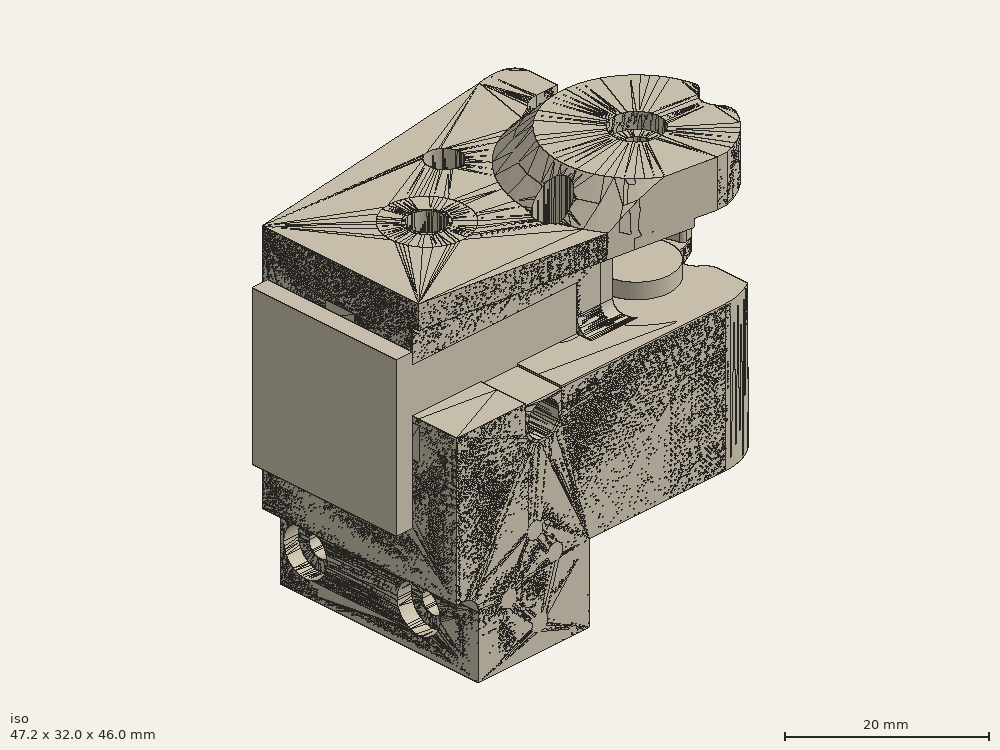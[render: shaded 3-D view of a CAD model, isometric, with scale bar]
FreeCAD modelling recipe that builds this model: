
FCSTD DOCUMENT  (FreeCAD 0.18R16146 (Git))
Label: carrier-right-2
License: All rights reserved
LicenseURL: http://en.wikipedia.org/wiki/All_rights_reserved
objects: Part::Cylinder×19, Part::Box×10, Part::Cut×10, Part::MultiFuse×9, Part::Feature×7, Part::Chamfer×6, Mesh::Feature×1
note: 61 computed .brp shape members not serialized (recipe doc carries the construction recipe); baked Part::Feature solids carry a one-line shape summary decoded from their .brp

FEATURE [Part::Box] Box003  label="Cube003"
  AttacherType = Attacher::AttachEngine3D
  Height = 2
  Length = 9
  Placement = pos=(-20.93,14.39,15.2) rot=(0,0,1;0rad)
  Width = 4
FEATURE [Part::Box] Box004  label="Cube004"
  AttacherType = Attacher::AttachEngine3D
  Height = 2
  Length = 9
  Placement = pos=(-5.93,14.39,15.2) rot=(0,0,1;0rad)
  Width = 4
FEATURE [Part::Box] Box005  label="Cube005"
  AttacherType = Attacher::AttachEngine3D
  Height = 2
  Length = 9
  Placement = pos=(-5.93,14.39,35.2) rot=(0,0,1;0rad)
  Width = 4
FEATURE [Part::Box] Box006  label="Cube006"
  AttacherType = Attacher::AttachEngine3D
  Height = 2
  Length = 9
  Placement = pos=(-20.93,14.39,35.2) rot=(0,0,1;0rad)
  Width = 4
FEATURE [Part::Box] Box007  label="Cube007"
  AttacherType = Attacher::AttachEngine3D
  Height = 4.2
  Length = 9
  Placement = pos=(-20.93,5.39,24) rot=(0,0,1;0rad)
  Width = 2
FEATURE [Part::Box] Box008  label="Cube008"
  AttacherType = Attacher::AttachEngine3D
  Height = 4.2
  Length = 7
  Placement = pos=(-5.93,5.39,24) rot=(0,0,1;0rad)
  Width = 2
FEATURE [Part::Chamfer] Chamfer
  Base = -> Box008
  Edges = 1 edges r=1: [Edge11]
FEATURE [Part::Chamfer] Chamfer001
  Base = -> Box007
  Edges = 1 edges r=1: [Edge11]
FEATURE [Part::MultiFuse] Fusion
  Shapes = -> [Chamfer001,Chamfer,Box006,Box005,Box004,Box003]
FEATURE [Part::Feature] Part__Feature199  label="Y_Carriage_RIGHT_Body (1)"
  Placement = pos=(-664.031,179.424,-461.938) rot=(1,0,0;1.5708rad)
  shape: bbox 48.82 x 34.51 x 45.95 mm, 173 faces (baked)
FEATURE [Part::Cylinder] Cylinder  label="ois-1"
  Angle = 360
  AttacherType = Attacher::AttachEngine3D
  Height = 2
  Placement = pos=(13.89,10.12,28.95) rot=(0,0,1;0rad)
  Radius = 4.5
FEATURE [Part::Cylinder] Cylinder009
  Angle = 360
  AttacherType = Attacher::AttachEngine3D
  Height = 0.75
  Placement = pos=(13.89,10.12,28.7) rot=(0,0,1;0rad)
  Radius = 1.5
FEATURE [Part::Cylinder] Cylinder010
  Angle = 360
  AttacherType = Attacher::AttachEngine3D
  Height = 0.75
  Placement = pos=(13.89,10.12,28.7) rot=(0,0,1;0rad)
  Radius = 3.5
FEATURE [Part::Cylinder] Cylinder011
  Angle = 360
  AttacherType = Attacher::AttachEngine3D
  Height = 0.75
  Placement = pos=(16.18,23.33,17.7) rot=(0,0,1;0rad)
  Radius = 3
FEATURE [Part::Cylinder] Cylinder012
  Angle = 360
  AttacherType = Attacher::AttachEngine3D
  Height = 11
  Placement = pos=(16.18,23.33,17.7) rot=(0,0,1;0rad)
  Radius = 10
FEATURE [Part::Cylinder] Cylinder013
  Angle = 360
  AttacherType = Attacher::AttachEngine3D
  Height = 0.75
  Placement = pos=(16.18,23.33,17.7) rot=(0,0,1;0rad)
  Radius = 1.5
FEATURE [Mesh::Feature] carrier_right  label="carrier-right"
FEATURE [Part::Feature] Part__Feature113  label="Y_CarriageHT_RIGHT_Body (1)"
  Placement = pos=(-664.031,179.424,-461.938) rot=(1,0,0;1.5708rad)
  shape: bbox 48.82 x 34.51 x 45.95 mm, 188 faces (baked)
FEATURE [Part::Box] Box010  label="Cube010"
  AttacherType = Attacher::AttachEngine3D
  Height = 20
  Length = 25
  Placement = pos=(-23.16,6.39,16.2) rot=(0,0,1;0rad)
  Width = 20
FEATURE [Part::Cylinder] Cylinder015
  Angle = 360
  AttacherType = Attacher::AttachEngine3D
  Height = 2
  Placement = pos=(13.89,10.12,38.2) rot=(0,0,1;0rad)
  Radius = 4.5
FEATURE [Part::Cylinder] Cylinder016
  Angle = 360
  AttacherType = Attacher::AttachEngine3D
  Height = 2
  Placement = pos=(13.89,10.12,28.7) rot=(0,0,1;0rad)
  Radius = 8
FEATURE [Part::Cylinder] Cylinder017
  Angle = 360
  AttacherType = Attacher::AttachEngine3D
  Height = 2
  Placement = pos=(13.89,10.12,38.2) rot=(0,0,1;0rad)
  Radius = 8
FEATURE [Part::Cut] Cut006003004
  Base = -> Cylinder010
  Tool = -> Cylinder009
FEATURE [Part::Feature] Cut006003004001  label="Cut006003005"
  Placement = pos=(0,0,10.75) rot=(0,0,1;0rad)
  shape: bbox 7 x 7 x 0.75 mm, 4 faces (baked)
FEATURE [Part::Chamfer] Chamfer002
  Base = -> Cut006003004001
  Edges = 1 edges r=0.5: [Edge3]
  Placement = pos=(0,0,0.1) rot=(0,0,1;0rad)
FEATURE [Part::Chamfer] Chamfer003
  Base = -> Cut006003004
  Edges = 1 edges r=0.5: [Edge1]
  Placement = pos=(0,0,-0.1) rot=(0,0,1;0rad)
FEATURE [Part::Cylinder] Cylinder014
  Angle = 360
  AttacherType = Attacher::AttachEngine3D
  Height = 5
  Placement = pos=(20.97,23.88,17) rot=(0,0,1;1.5708rad)
  Radius = 3
FEATURE [Part::Cut] Cut006003004003
  Base = -> Cylinder011
  Tool = -> Cylinder013
FEATURE [Part::Feature] Cut006003004003001  label="Cut006003004004"
  Placement = pos=(0,0,10.6) rot=(0,0,1;0rad)
  shape: bbox 6 x 6 x 0.75 mm, 4 faces (baked)
FEATURE [Part::Feature] Cut006003004003002  label="Cut006003004005"
  Placement = pos=(0,0,-0.35) rot=(0,0,1;0rad)
  shape: bbox 6 x 6 x 0.75 mm, 4 faces (baked)
FEATURE [Part::Chamfer] Chamfer004
  Base = -> Cut006003004003002
  Edges = 1 edges r=0.5: [Edge1]
FEATURE [Part::Cut] Cut006003004003003
  Base = -> Chamfer004
  Tool = -> Cylinder014
FEATURE [Part::Chamfer] Chamfer005
  Base = -> Cut006003004003001
  Edges = 1 edges r=0.5: [Edge3]
FEATURE [Part::Box] Box  label="Cube"
  AttacherType = Attacher::AttachEngine3D
  Height = 10
  Length = 10
  Placement = pos=(19.07,19.6,23.8) rot=(0,0,1;0rad)
  Width = 10
FEATURE [Part::Cut] Cut006003004003004
  Base = -> Chamfer005
  Tool = -> Box
FEATURE [Part::MultiFuse] Fusion001
  Shapes = -> [Cut006003004003004,Cut006003004003003,Chamfer002,Chamfer003]
FEATURE [Part::Feature] Fusion003001_solid  label="rev-1-exp"
  shape: bbox 48.82 x 34.51 x 45.95 mm, 242 faces (baked)
FEATURE [Part::Cut] Cut
  Base = -> Fusion003001_solid
  Tool = -> Cylinder016
FEATURE [Part::Cut] Cut006003004003005
  Base = -> Cut
  Tool = -> Cylinder017
FEATURE [Part::Cut] Cut006003004003006
  Base = -> Cut006003004003005
  Tool = -> Cylinder012
FEATURE [Part::MultiFuse] Fusion002  label="std-r1"
  Shapes = -> [Cut006003004003006,Fusion001]
FEATURE [Part::Cylinder] Cylinder018
  Angle = 360
  AttacherType = Attacher::AttachEngine3D
  Height = 6
  Placement = pos=(13.89,10.12,10) rot=(0,0,1;0rad)
  Radius = 2.1
FEATURE [Part::Cylinder] Cylinder020
  Angle = 360
  AttacherType = Attacher::AttachEngine3D
  Height = 6
  Placement = pos=(16.18,23.33,10) rot=(0,0,1;0rad)
  Radius = 2.1
FEATURE [Part::Cylinder] Cylinder021
  Angle = 360
  AttacherType = Attacher::AttachEngine3D
  Height = 5
  Placement = pos=(20.97,23.88,15.2) rot=(0,0,1;1.5708rad)
  Radius = 3
FEATURE [Part::Cylinder] Cylinder022
  Angle = 360
  AttacherType = Attacher::AttachEngine3D
  Height = 6
  Placement = pos=(13.89,10.12,10) rot=(0,0,1;0rad)
  Radius = 3.3
FEATURE [Part::Cylinder] Cylinder023
  Angle = 360
  AttacherType = Attacher::AttachEngine3D
  Height = 6
  Placement = pos=(16.18,23.33,10) rot=(0,0,1;0rad)
  Radius = 3.3
FEATURE [Part::Feature] Fusion002_solid  label="Fusion002 (Solid)"
  shape: bbox 48.82 x 34.51 x 45.95 mm, 267 faces (baked)
FEATURE [Part::MultiFuse] Fusion003
  Shapes = -> [Cylinder022,Cylinder023,Fusion002_solid]
FEATURE [Part::MultiFuse] Fusion004
  Shapes = -> [Cylinder020,Cylinder018]
FEATURE [Part::Cut] Cut006003004003007
  Base = -> Fusion003
  Tool = -> Fusion004
FEATURE [Part::Cut] Cut006003004003008  label="insert-r1"
  Base = -> Cut006003004003007
  Tool = -> Cylinder021
FEATURE [Part::Cylinder] Cylinder024  label="Cylinder"
  Angle = 360
  AttacherType = Attacher::AttachEngine3D
  Height = 6.1
  Placement = pos=(-2.43,8.54,5) rot=(0,1,0;4.71239rad)
  Radius = 2.1
FEATURE [Part::Cylinder] Cylinder025  label="Cylinder024"
  Angle = 360
  AttacherType = Attacher::AttachEngine3D
  Height = 6.1
  Placement = pos=(-2.43,24.24,5) rot=(0,-1,0;1.5708rad)
  Radius = 2.1
FEATURE [Part::Cylinder] Cylinder026  label="Cylinder027"
  Angle = 360
  AttacherType = Attacher::AttachEngine3D
  Height = 28.1
  Placement = pos=(-2.43,24.24,5) rot=(0,-1,0;1.5708rad)
  Radius = 1.65
FEATURE [Part::Cylinder] Cylinder027  label="Cylinder028"
  Angle = 360
  AttacherType = Attacher::AttachEngine3D
  Height = 28.1
  Placement = pos=(-2.43,8.54,5) rot=(0,-1,0;1.5708rad)
  Radius = 1.65
FEATURE [Part::MultiFuse] Fusion005
  Shapes = -> [Cylinder025,Cylinder024]
FEATURE [Part::MultiFuse] Fusion006
  Shapes = -> [Cylinder027,Cylinder026]
FEATURE [Part::MultiFuse] Fusion007
  Shapes = -> [Fusion006,Fusion005]
FEATURE [Part::Box] Box011  label="Cube011"
  AttacherType = Attacher::AttachEngine3D
  Height = 9
  Length = 4
  Placement = pos=(-10,5.3,0) rot=(0,0,1;0rad)
  Width = 6
FEATURE [Part::Box] Box012  label="Cube012"
  AttacherType = Attacher::AttachEngine3D
  Height = 9
  Length = 4
  Placement = pos=(-10,21.4,0) rot=(0,0,1;0rad)
  Width = 6
FEATURE [Part::MultiFuse] Fusion008
  Shapes = -> [Box012,Box011,Cut006003004003008]
FEATURE [Part::Cut] Cut006003004003009
  Base = -> Fusion008
  Tool = -> Fusion007
